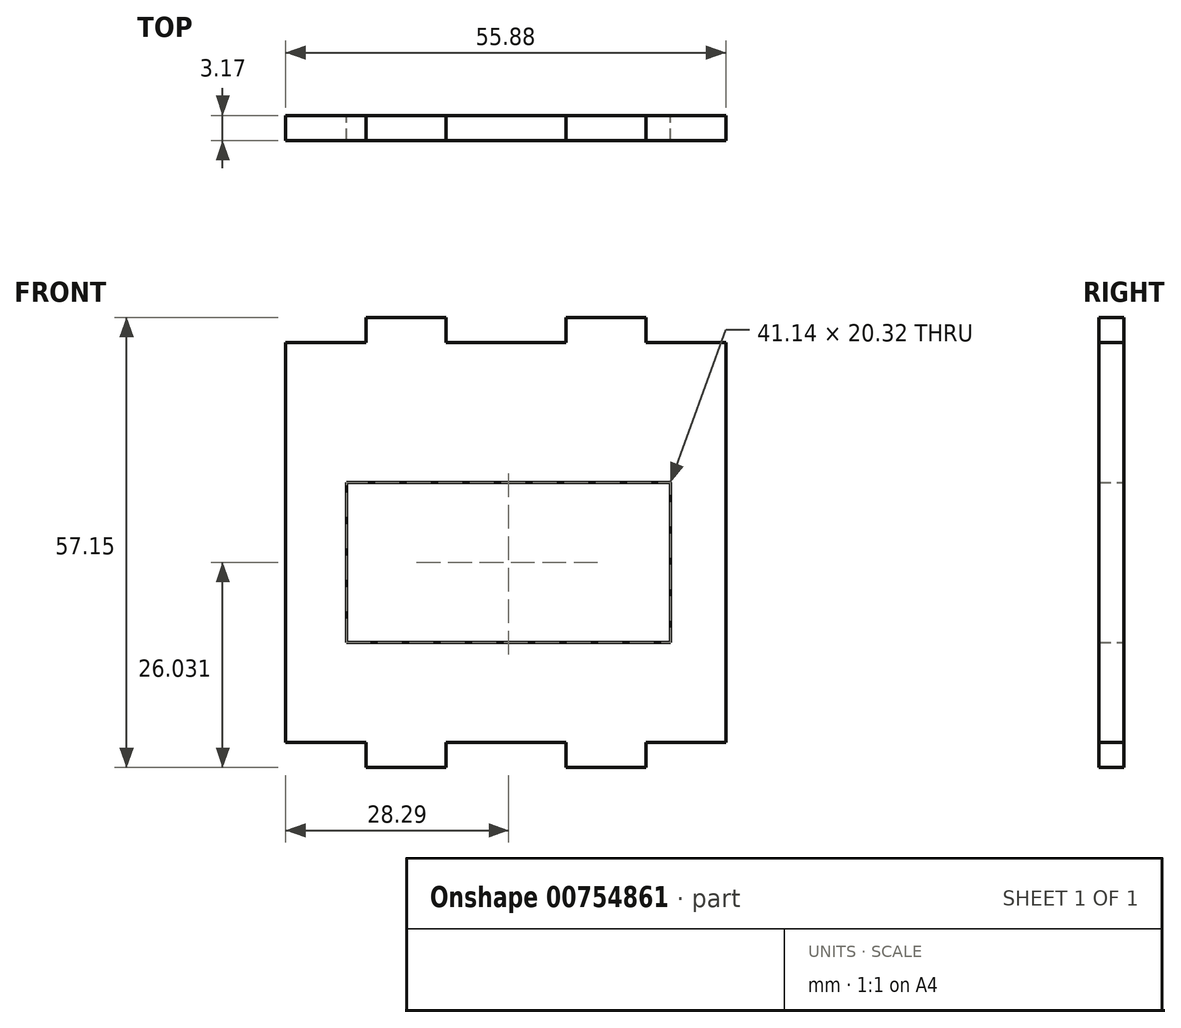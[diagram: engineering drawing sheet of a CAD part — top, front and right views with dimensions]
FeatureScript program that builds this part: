
annotation { "Feature Type Name" : "Feature", "Feature Type Description" : "" }
export const myFeature = defineFeature(function(context is Context, id is Id, definition is map)
    precondition{}
    {
        {
            var Q0;
            Q0=qCreatedBy(makeId("Front.planeOp"),FACE);
            var sketch = newSketch(context, id + "F0", { "sketchPlane" : qUnion([Q0])});
            skLineSegment(sketch, "E0.bottom", {"start": v(-60.87, 13.18) * mm, "end": v(-50.7, 13.18) * mm});
            skLineSegment(sketch, "E0.top", {"start": v(-60.87, -37.62) * mm, "end": v(-50.7, -37.62) * mm});
            skLineSegment(sketch, "E0.left", {"start": v(-60.87, 13.18) * mm, "end": v(-60.87, -37.62) * mm});
            skLineSegment(sketch, "E0.right", {"start": v(-4.99, 13.18) * mm, "end": v(-4.99, -37.62) * mm});
            skLineSegment(sketch, "E1.top", {"start": v(-50.7, -40.8) * mm, "end": v(-40.55, -40.8) * mm});
            skLineSegment(sketch, "E1.left", {"start": v(-50.7, -37.62) * mm, "end": v(-50.7, -40.8) * mm});
            skLineSegment(sketch, "E1.right", {"start": v(-40.55, -37.62) * mm, "end": v(-40.55, -40.8) * mm});
            skLineSegment(sketch, "E2.top", {"start": v(-25.3, -40.8) * mm, "end": v(-15.15, -40.8) * mm});
            skLineSegment(sketch, "E2.left", {"start": v(-25.3, -37.62) * mm, "end": v(-25.3, -40.8) * mm});
            skLineSegment(sketch, "E2.right", {"start": v(-15.15, -37.62) * mm, "end": v(-15.15, -40.8) * mm});
            skLineSegment(sketch, "E3.trimOffspring", {"start": v(-15.15, -37.62) * mm, "end": v(-4.99, -37.62) * mm});
            skLineSegment(sketch, "E4.trimOffspring", {"start": v(-40.55, -37.62) * mm, "end": v(-25.3, -37.62) * mm});
            skLineSegment(sketch, "E5.MirrorCS", {"start": v(-50.7, 16.36) * mm, "end": v(-40.55, 16.36) * mm});
            skLineSegment(sketch, "E6.MirrorCS", {"start": v(-25.3, 16.36) * mm, "end": v(-15.15, 16.36) * mm});
            skLineSegment(sketch, "E7", {"start": v(-50.7, 16.36) * mm, "end": v(-50.7, 13.18) * mm});
            skLineSegment(sketch, "E8", {"start": v(-40.55, 16.36) * mm, "end": v(-40.55, 13.18) * mm});
            skLineSegment(sketch, "E9", {"start": v(-25.3, 16.36) * mm, "end": v(-25.3, 13.18) * mm});
            skLineSegment(sketch, "E10", {"start": v(-15.15, 13.18) * mm, "end": v(-15.15, 16.36) * mm});
            skLineSegment(sketch, "E11.trimOffspring", {"start": v(-40.55, 13.18) * mm, "end": v(-25.3, 13.18) * mm});
            skLineSegment(sketch, "E12.trimOffspring", {"start": v(-15.15, 13.18) * mm, "end": v(-4.99, 13.18) * mm});
            skPoint(sketch, "E13.end.orphan", {"position": v(-4.99, -12.22) * mm});
            skPoint(sketch, "E13.start.orphan", {"position": v(-60.87, -12.22) * mm});
            skLineSegment(sketch, "E14.bottom", {"start": v(-53.15, -4.6) * mm, "end": v(-12, -4.6) * mm});
            skLineSegment(sketch, "E14.top", {"start": v(-53.15, -24.92) * mm, "end": v(-12, -24.92) * mm});
            skLineSegment(sketch, "E14.left", {"start": v(-53.15, -4.6) * mm, "end": v(-53.15, -24.92) * mm});
            skLineSegment(sketch, "E14.right", {"start": v(-12, -4.6) * mm, "end": v(-12, -24.92) * mm});
            skSolve(sketch);
        }
        {
            var Q0;
            Q0=makeQuery(id+"F0.imprint","IMPRINT",FACE,{"disambiguationData":[TD([[makeQuery(id+"F0.imprint","IMPRINT",EDGE,{"derivedFrom":sQuery(id+"F0.wireOp",EDGE,"E0.bottom")}),-1.0]])]});
            extrude(context, id + "F1", {"entities" : qUnion([Q0]), "depth" : 3.17 * mm, "offsetDistance" : 25.4 * mm});
        }
    });
